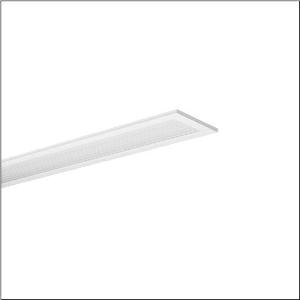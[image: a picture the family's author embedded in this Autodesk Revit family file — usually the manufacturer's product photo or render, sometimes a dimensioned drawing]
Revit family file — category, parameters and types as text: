
# Revit family: apollon_r__21_linear_51mq15wd2414_32e0
name_source: partatom
category: Lighting Fixtures
units: mm (PartAtom-declared; Revit-internal decimal feet)

## family parameters
Cut with Voids When Loaded = No
Host = Face
Light Source = No
Part Type = Normal
Room Calculation Point = No
Round Connector Dimension = Use Diameter
Shared = No

## types (1)
- Apollon® 21 linear (1 x LED, 2520 lm, 17.4 W, 4000K)
    Apparent Load = 17 VA
    CIE Flux Codes = 66 89 97 100 100
    Color Rendering = 80
    Color Temperature = 4000K
    Default Elevation = 1800 mm
    Description = Apollon® 21 linear, office luminaire, primary optical cover: micro prismatic cover, of PMMA, CAT 2 (L<= 3000cd/m²), light emission: direct distribution, primary light characteristic: symmetric, installation type: lay-in mounting, LED, rated luminous flux: 2.520lm, luminous efficacy: 145lm/W, light colour: 840, colour temperature: 4000K, with terminal, 5-pole, mains connection: 220..240V, AC/DC, 0/50..60Hz, rated input power: 17.4W, housing, of aluminium, coated, traffic white (RAL 9016), length: 1.245mm, width: 179mm, height: 30mm, housing upper side, of sheet steel, galvanised, protection rating (complete): IP20, protection rating (lamp compartment, on room side): IP50, insulation class (complete): insulation class II (safety insulation), certification: CE, ENEC, impact resistance: IK03, permissible operating ambient temperature: -20..+45°C, permissible storage temperature: -40..+80°C, packaging unit: 1 piece
    Height = 0 mm  [stored 0 ft]
    Lamp = 1 x LED
    Lamp Light Flux = 2520 lm
    Lamp Power = 17.4 W
    Lamp count = 1
    Length = 1245 mm
    Luminous efficacy = 145 lm/W
    Manufacturer = Siteco
    ModVariant = No
    Model = 51MQ15WD2414
    Mounting Place = Ceiling
    Mounting Type = Recessed
    Number of Poles = 1
    OnlyDefault = Yes
    Power Factor = 1
    Product Name = Apollon® 21 linear
    Product group = office luminaire | ceiling recessed
    ProductGroupID = 401
    Protection Class = Protection class II
    Protection Degree = IP 20
    RLX_Detail_Level = 1
    RLX_Emergency_Light_Flux = 0 lm
    RLX_Emergency_Type = 0
    RLX_Emergency_Type_DB = No
    RlxData = <blob elided: 12525 chars, md5=0564b6b8>
    Socket = socket
    Standby Power = 0 W
    System Light Flux = 2520 lm
    System Power = 17 W
    Type Comments = Product without accessories
    Type Image = l_1291018.jpg
    URL = http://relux.com
    VarID = ---
    Voltage = 0 V
    Weight = 0.00 kg
    Width = 179 mm

note: [stored X ft] marks values corroborated as IEEE doubles in the binary element streams (Revit-internal decimal feet)

## geometry (parser evidence)
native form markers: Sweep x10
no freeform markers — native parametric forms only
